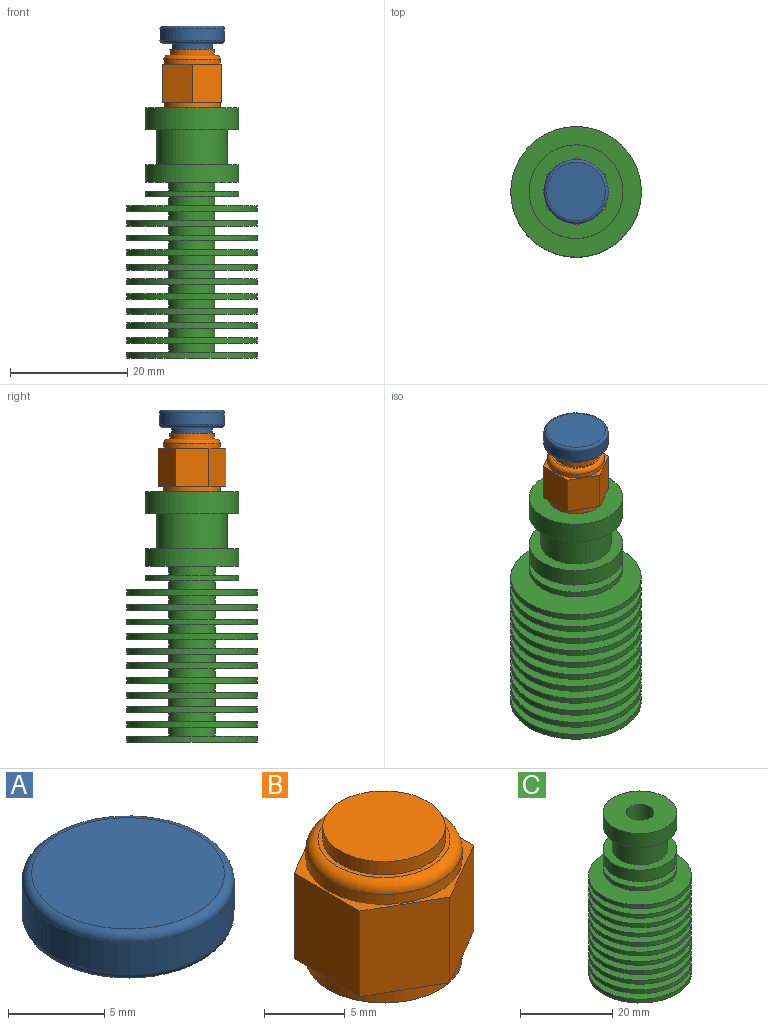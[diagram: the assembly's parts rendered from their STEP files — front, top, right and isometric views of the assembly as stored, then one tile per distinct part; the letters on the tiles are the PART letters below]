
ASSEMBLY  parts=3 mates=2
PART A: 7 faces, bbox 11.9x11.9x4 mm
  f0: cylinder r=3.5mm len=7mm, axis (0,0,-1), area 22mm2, adj f1,f4
  f1: plane 7x7mm, normal (0,0,-1), area 38.5mm2, adj f0
  f2: cylinder r=5.5mm len=11mm, axis (0,0,-1), area 69.1mm2, adj f5,f6
  f3: plane 10x10mm, normal (0,0,1), area 78.5mm2, adj f6
  f4: plane 10x10mm, normal (0,0,-1), area 40.1mm2, adj f0,f5
  f5: torus R=5mm, axis (0,0,1), area 26.2mm2, adj f2,f4
  f6: torus R=5mm, axis (0,0,1), area 26.2mm2, adj f2,f3
PART B: 15 faces, bbox 10.5x11.5x10 mm
  f0: cylinder r=4.85mm len=9.7mm, axis (0,0,1), area 30.5mm2, adj f1,f9
  f1: plane 9.7x9.7mm, normal (0,0,-1), area 73.9mm2, adj f0
  f2: plane 6.5x5mm, normal (0.5,0.87,0), area 37.5mm2, adj f3,f7,f8,f9
  f3: plane 6.5x5mm, normal (-0.5,0.87,0), area 37.5mm2, adj f2,f4,f8,f9
  f4: plane 6.5x5.77mm, normal (-1,0,0), area 37.5mm2, adj f3,f5,f8,f9
  f5: plane 6.5x5mm, normal (-0.5,-0.87,0), area 37.5mm2, adj f4,f6,f8,f9
  f6: plane 6.5x5mm, normal (0.5,-0.87,0), area 37.5mm2, adj f5,f7,f8,f9
  f7: plane 6.5x5.77mm, normal (1,0,0), area 37.5mm2, adj f2,f6,f8,f9
  f8: plane 11.55x10mm, normal (0,0,1), area 12.7mm2, adj f2,f3,f4,f5,f6,f7,f10
  f9: plane 11.55x10mm, normal (0,0,-1), area 12.7mm2, adj f0,f2,f3,f4,f5,f6,f7
  f10: cylinder r=4.85mm len=9.7mm, axis (0,0,-1), area 22.9mm2, adj f8,f12
  f11: plane 8.2x8.2mm, normal (0,0,1), area 7.4mm2, adj f12,f13
  f12: torus R=4.1mm, axis (0,0,1), area 33.9mm2, adj f10,f11
  f13: cylinder r=3.8mm len=7.6mm, axis (0,0,-1), area 23.9mm2, adj f11,f14
  f14: plane 7.6x7.6mm, normal (0,0,1), area 45.4mm2, adj f13
PART C: 56 faces, bbox 22.3x22.3x42.7 mm
  f0: plane 16x16mm, normal (0,0,-1), area 150.8mm2, adj f1,f55
  f1: cylinder r=4mm len=8mm, axis (0,0,-1), area 37.7mm2, adj f0,f2
  f2: plane 16x16mm, normal (0,0,1), area 150.8mm2, adj f1,f3
  f3: cylinder r=8mm len=16mm, axis (0,0,-1), area 50.3mm2, adj f2,f4
  f4: plane 16x16mm, normal (0,0,-1), area 150.8mm2, adj f3,f5
  f5: cylinder r=4mm len=8mm, axis (0,0,-1), area 37.7mm2, adj f4,f6
  f6: plane 22.3x22.3mm, normal (0,0,1), area 340.3mm2, adj f5,f7
  f7: cylinder r=11.15mm len=22.3mm, axis (0,0,-1), area 70.1mm2, adj f6,f8
  f8: plane 22.3x22.3mm, normal (0,0,-1), area 340.3mm2, adj f7,f9
  f9: cylinder r=4mm len=8mm, axis (0,0,-1), area 37.7mm2, adj f8,f10
  f10: plane 22.3x22.3mm, normal (0,0,1), area 340.3mm2, adj f9,f11
  f11: cylinder r=11.15mm len=22.3mm, axis (0,0,-1), area 70.1mm2, adj f10,f12
  f12: plane 22.3x22.3mm, normal (0,0,-1), area 340.3mm2, adj f11,f13
  f13: cylinder r=4mm len=8mm, axis (0,0,-1), area 37.7mm2, adj f12,f14
  f14: plane 22.3x22.3mm, normal (0,0,1), area 340.3mm2, adj f13,f15
  f15: cylinder r=11.15mm len=22.3mm, axis (0,0,-1), area 70.1mm2, adj f14,f16
  f16: plane 22.3x22.3mm, normal (0,0,-1), area 340.3mm2, adj f15,f17
  f17: cylinder r=4mm len=8mm, axis (0,0,-1), area 37.7mm2, adj f16,f18
  f18: plane 22.3x22.3mm, normal (0,0,1), area 340.3mm2, adj f17,f19
  f19: cylinder r=11.15mm len=22.3mm, axis (0,0,-1), area 70.1mm2, adj f18,f20
  f20: plane 22.3x22.3mm, normal (0,0,-1), area 340.3mm2, adj f19,f21
  f21: cylinder r=4mm len=8mm, axis (0,0,-1), area 37.7mm2, adj f20,f22
  f22: plane 22.3x22.3mm, normal (0,0,1), area 340.3mm2, adj f21,f23
  f23: cylinder r=11.15mm len=22.3mm, axis (0,0,-1), area 70.1mm2, adj f22,f24
  f24: plane 22.3x22.3mm, normal (0,0,-1), area 340.3mm2, adj f23,f25
  f25: cylinder r=4mm len=8mm, axis (0,0,-1), area 37.7mm2, adj f24,f26
  f26: plane 22.3x22.3mm, normal (0,0,1), area 340.3mm2, adj f25,f27
  f27: cylinder r=11.15mm len=22.3mm, axis (0,0,-1), area 70.1mm2, adj f26,f28
  f28: plane 22.3x22.3mm, normal (0,0,-1), area 340.3mm2, adj f27,f29
  f29: cylinder r=4mm len=8mm, axis (0,0,-1), area 37.7mm2, adj f28,f30
  f30: plane 22.3x22.3mm, normal (0,0,1), area 340.3mm2, adj f29,f31
  f31: cylinder r=11.15mm len=22.3mm, axis (0,0,-1), area 70.1mm2, adj f30,f32
  f32: plane 22.3x22.3mm, normal (0,0,-1), area 340.3mm2, adj f31,f33
  f33: cylinder r=4mm len=8mm, axis (0,0,-1), area 37.7mm2, adj f32,f34
  f34: plane 22.3x22.3mm, normal (0,0,1), area 340.3mm2, adj f33,f35
  f35: cylinder r=11.15mm len=22.3mm, axis (0,0,-1), area 70.1mm2, adj f34,f36
  f36: plane 22.3x22.3mm, normal (0,0,-1), area 340.3mm2, adj f35,f37
  f37: cylinder r=4mm len=8mm, axis (0,0,-1), area 37.7mm2, adj f36,f38
  f38: plane 22.3x22.3mm, normal (0,0,1), area 340.3mm2, adj f37,f39
  f39: cylinder r=11.15mm len=22.3mm, axis (0,0,-1), area 70.1mm2, adj f38,f40
  f40: plane 22.3x22.3mm, normal (0,0,-1), area 340.3mm2, adj f39,f41
  f41: cylinder r=4mm len=8mm, axis (0,0,-1), area 37.7mm2, adj f40,f42
  f42: plane 22.3x22.3mm, normal (0,0,1), area 340.3mm2, adj f41,f43
  f43: cylinder r=11.15mm len=22.3mm, axis (0,0,-1), area 70.1mm2, adj f42,f44
  f44: plane 22.3x22.3mm, normal (0,0,-1), area 340.3mm2, adj f43,f45
  f45: cylinder r=4mm len=8mm, axis (0,0,-1), area 37.7mm2, adj f44,f46
  f46: plane 22.3x22.3mm, normal (0,0,1), area 340.3mm2, adj f45,f47
  f47: cylinder r=11.15mm len=22.3mm, axis (0,0,-1), area 70.1mm2, adj f46,f48
  f48: plane 22.3x22.3mm, normal (0,0,-1), area 362.3mm2, adj f47,f49
  f49: cylinder r=3mm len=42.7mm, axis (0,0,-1), area 804.9mm2, adj f48,f50
  f50: plane 16x16mm, normal (0,0,1), area 172.8mm2, adj f49,f51
  f51: cylinder r=8mm len=16mm, axis (0,0,-1), area 186mm2, adj f50,f52
  f52: plane 16x16mm, normal (0,0,-1), area 88mm2, adj f51,f53
  f53: cylinder r=6mm len=12mm, axis (0,0,-1), area 226.2mm2, adj f52,f54
  f54: plane 16x16mm, normal (0,0,1), area 88mm2, adj f53,f55
  f55: cylinder r=8mm len=16mm, axis (0,0,-1), area 150.8mm2, adj f0,f54
PLACE A t=(-12.25,9.27,-18.99)mm
PLACE B t=(-12.25,9.27,-18.99)mm
PLACE C t=(-12.25,9.27,-18.99)mm
MATE fastened C.f1 <-> B.f0  axis (0,0,1) through (-12.25,9.27,-18.99)mm
MATE fastened B.f0 <-> A.f0  axis (0,0,1) through (-12.25,9.27,-8.99)mm
